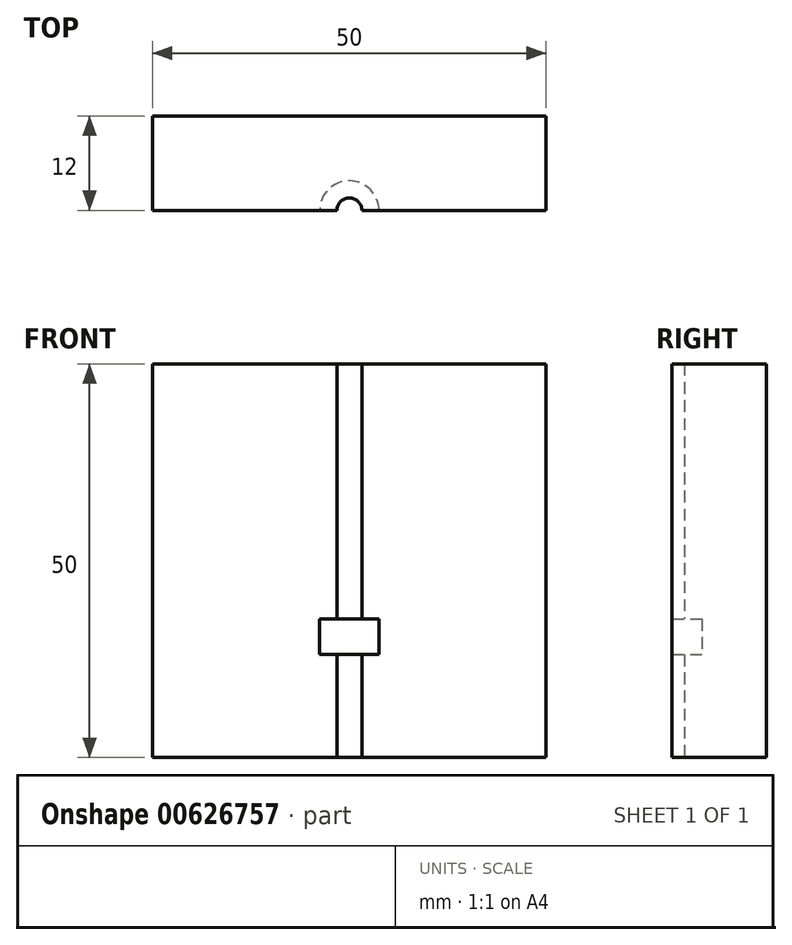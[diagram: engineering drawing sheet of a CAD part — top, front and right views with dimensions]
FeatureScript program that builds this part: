
annotation { "Feature Type Name" : "Feature", "Feature Type Description" : "" }
export const myFeature = defineFeature(function(context is Context, id is Id, definition is map)
    precondition{}
    {
        {
            var Q0;
            Q0=qCreatedBy(makeId("Top.planeOp"),FACE);
            var sketch = newSketch(context, id + "F0", { "sketchPlane" : qUnion([Q0])});
            skCircle(sketch, "E0", {"center": v(0, 0) * mm, "radius": 1.59 * mm});
            skCircle(sketch, "E1", {"center": v(0, 0) * mm, "radius": 3.77 * mm});
            skLineSegment(sketch, "E2.bottom", {"start": v(25, 12) * mm, "end": v(-25, 12) * mm});
            skLineSegment(sketch, "E2.top", {"start": v(25, 0) * mm, "end": v(-25, 0) * mm});
            skLineSegment(sketch, "E2.left", {"start": v(25, 12) * mm, "end": v(25, 0) * mm});
            skLineSegment(sketch, "E2.right", {"start": v(-25, 12) * mm, "end": v(-25, 0) * mm});
            skPoint(sketch, "E2.middle", {"position": v(0, 6) * mm});
            skSolve(sketch);
        }
        {
            var Q0;
            {var subQ0=sQuery(id+"F0.wireOp",EDGE,"E2.top");var subQ1=sQuery(id+"F0.wireOp",EDGE,"E0");var subQ2=makeQuery(id+"F0.imprint","INTERSECT",VERTEX,{"disambiguationData":[OD(0.0)],"derivedFrom":[subQ1,subQ0]});Q0=makeQuery(id+"F0.imprint","IMPRINT",FACE,{"disambiguationData":[TD([[makeQuery(id+"F0.imprint","IMPRINT",EDGE,{"disambiguationData":[TD([[subQ2,-1.0]])],"derivedFrom":subQ1}),-1.0]])]});}
            var Q1;
            Q1=makeQuery(id+"F0.imprint","IMPRINT",FACE,{"disambiguationData":[TD([[makeQuery(id+"F0.imprint","IMPRINT",EDGE,{"derivedFrom":sQuery(id+"F0.wireOp",EDGE,"E2.bottom")}),1.0]])]});
            extrude(context, id + "F1", {"entities" : qUnion([Q0, Q1]), "depth" : 50 * mm, "offsetDistance" : 25 * mm});
        }
        {
            var Q0;
            {var subQ0=sQuery(id+"F0.wireOp",EDGE,"E2.top");var subQ1=sQuery(id+"F0.wireOp",EDGE,"E0");var subQ2=makeQuery(id+"F0.imprint","INTERSECT",VERTEX,{"disambiguationData":[OD(0.0)],"derivedFrom":[subQ1,subQ0]});Q0=makeQuery(id+"F0.imprint","IMPRINT",FACE,{"disambiguationData":[TD([[makeQuery(id+"F0.imprint","IMPRINT",EDGE,{"disambiguationData":[TD([[subQ2,1.0]])],"derivedFrom":subQ1}),-1.0]])]});}
            var Q1;
            {var subQ0=sQuery(id+"F0.wireOp",EDGE,"E2.top");var subQ1=sQuery(id+"F0.wireOp",EDGE,"E0");var subQ2=makeQuery(id+"F0.imprint","INTERSECT",VERTEX,{"disambiguationData":[OD(0.0)],"derivedFrom":[subQ1,subQ0]});Q1=makeQuery(id+"F0.imprint","IMPRINT",FACE,{"disambiguationData":[TD([[makeQuery(id+"F0.imprint","IMPRINT",EDGE,{"disambiguationData":[TD([[subQ2,-1.0]])],"derivedFrom":subQ1}),-1.0]])]});}
            extrude(context, id + "F2", {"entities" : qUnion([Q0, Q1]), "operationType" : NewBodyOperationType.REMOVE, "depth" : (13.1 + 4.5) * mm, "offsetDistance" : 25 * mm, "hasSecondDirection" : true, "secondDirectionOppositeDirection" : false, "secondDirectionDepth" : 13.1 * mm});
        }
    });
